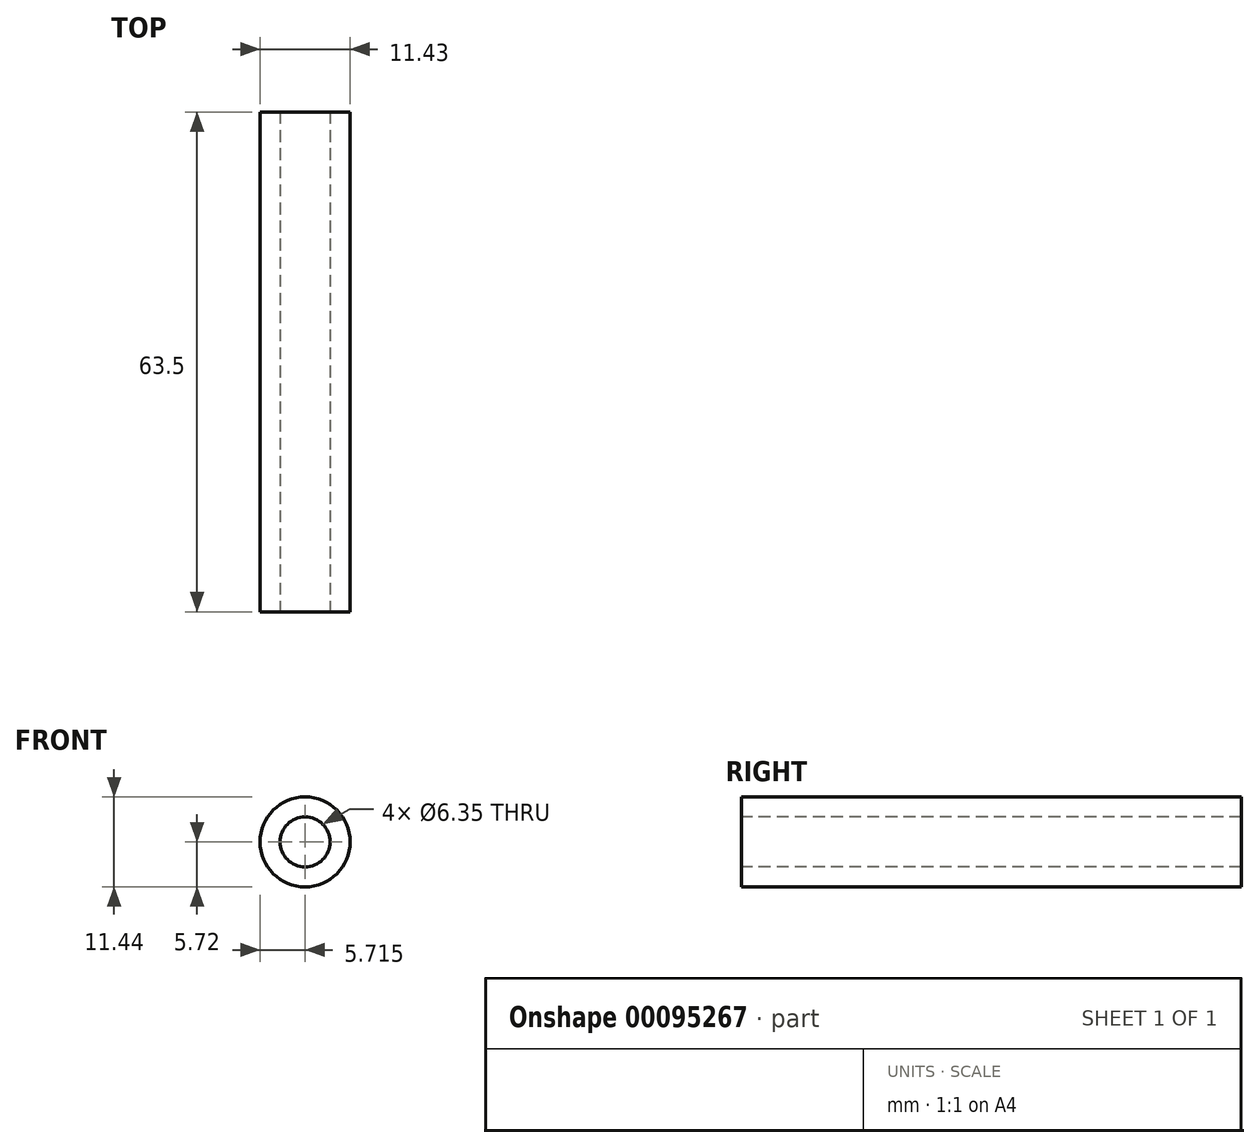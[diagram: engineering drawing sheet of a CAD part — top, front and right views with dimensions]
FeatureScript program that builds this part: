
annotation { "Feature Type Name" : "Feature", "Feature Type Description" : "" }
export const myFeature = defineFeature(function(context is Context, id is Id, definition is map)
    precondition{}
    {
        {
            var Q0;
            Q0=qCreatedBy(makeId("Front.planeOp"),FACE);
            var sketch = newSketch(context, id + "F0", { "sketchPlane" : qUnion([Q0])});
            skLineSegment(sketch, "E0", {"start": v(0, 0) * mm, "end": v(0, 12.7) * mm});
            skLineSegment(sketch, "E1", {"start": v(0, 12.7) * mm, "end": v(10.16, 12.7) * mm});
            skLineSegment(sketch, "E2", {"start": v(10.16, 12.7) * mm, "end": v(10.16, 10.16) * mm});
            skLineSegment(sketch, "E3", {"start": v(10.16, 10.16) * mm, "end": v(56.13, 10.16) * mm});
            skLineSegment(sketch, "E4", {"start": v(56.13, 10.16) * mm, "end": v(56.13, 12.7) * mm});
            skLineSegment(sketch, "E5", {"start": v(56.13, 12.7) * mm, "end": v(66.3, 12.7) * mm});
            skLineSegment(sketch, "E6", {"start": v(66.3, 12.7) * mm, "end": v(66.3, 0) * mm});
            skLineSegment(sketch, "E7", {"start": v(66.3, 0) * mm, "end": v(0, 0) * mm});
            skLineSegment(sketch, "E8", {"start": v(5.84, 15.24) * mm, "end": v(-0.5, 15.24) * mm});
            skLineSegment(sketch, "E9", {"start": v(-0.5, 15.24) * mm, "end": v(-10.88, 3.85) * mm});
            skLineSegment(sketch, "E10", {"start": v(0, 0) * mm, "end": v(-6.65, 0) * mm});
            skCircle(sketch, "E11", {"center": v(-6.65, 0) * mm, "radius": 5.72 * mm});
            skCircle(sketch, "E12", {"center": v(-6.65, 0) * mm, "radius": 3.18 * mm});
            skLineSegment(sketch, "E13", {"start": v(5.84, 15.24) * mm, "end": v(5.84, -9.4) * mm});
            skLineSegment(sketch, "E14", {"start": v(5.84, -9.4) * mm, "end": v(-8.18, -5.5) * mm});
            skSolve(sketch);
        }
        {
            var Q0;
            {var subQ4=sQuery(id+"F0.wireOp",EDGE,"E12");Q0=makeQuery(id+"F0.imprint","IMPRINT",FACE,{"disambiguationData":[TD([[makeQuery(id+"F0.imprint","IMPRINT",EDGE,{"derivedFrom":subQ4}),-1.0]])]});}
            extrude(context, id + "F1", {"entities" : qUnion([Q0]), "oppositeDirection" : true, "depth" : 63.5 * mm});
        }
    });
